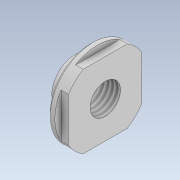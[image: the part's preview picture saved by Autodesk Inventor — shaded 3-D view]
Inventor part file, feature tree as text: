
AUTODESK INVENTOR PART (.ipt)
format: ipt  version: 2021 (Build 250183000, 183)  size: 133,120 bytes
history: native  units: mm
features: sketch x2, other x1, revolve x1, fillet x1, chamfer x1, extrude x1, thread x1
ambient origin geometry x8: Origin, YZ Plane, XZ Plane, XY Plane, X Axis, Y Axis, Z Axis, Center Point
bodies: Body1 (feature_tree)
feature tree (8):
  other  "Sólido1"
  revolve  "Revolución1"  [1 undecoded]
  fillet  "Empalme1"  Radius=28.0mm
  chamfer  "Chaflán1"  Distance=10.0mm
  extrude  "Extrusión1"  TaperAngle=90.0deg  [1 undecoded]
  thread  "Rosca1"  [1 undecoded]
  sketch  "Boceto1"  dims[d0=5.0mm d1=5.0mm d3=28.0mm]
  sketch  "Boceto2"  dims[d4=15.0mm d5=10.0mm d6=90.0deg d7=1.0mm d8=1.0mm d9=2.0mm d10=45.0deg d11=24.0mm d12=24.0mm d13=2.5mm d14=0.0mm d15=20.0mm d16=0.0mm]
note: 3 required parameter values undecoded (feature->parameter linkage not recoverable at this tier; creation-order binding heuristic only, values carry confidence <= 0.55)